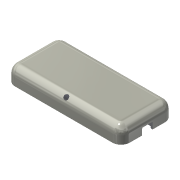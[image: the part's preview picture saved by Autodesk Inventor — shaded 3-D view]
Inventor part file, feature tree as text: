
AUTODESK INVENTOR PART (.ipt)
format: ipt  version: 2022.1 (Build 261234020, 234B)  size: 246,272 bytes
history: native  units: mm
features: extrude x6, fillet x5, sketch x4, plane x2, other x1, projected_geometry x1
ambient origin geometry x8: Origin, YZ Plane, XZ Plane, XY Plane, X Axis, Y Axis, Z Axis, Center Point
bodies: Solid1 (feature_tree)
feature tree (19):
  sketch  "Sketch1"  dims[d0=120.0mm d1=55.0mm]
  extrude  "Extrusion1"  Depth=55.0mm
  extrude  "Extrusion2"  Depth=10.0mm
  fillet  "Fillet3"  Radius=15.0mm
  fillet  "Fillet4"  Radius=10.0mm
  fillet  "Fillet5"  Radius=9.0mm
  other  "Lip3"
  fillet  "Fillet6"  Radius=9.0mm
  extrude  "Extrusion6"  Depth=10.0mm
  fillet  "Fillet7"  Radius=5.5mm
  extrude  "Extrusion7"  Depth=10.0mm
  plane  "Work Plane1"
  plane  "Work Plane2"
  sketch  "Sketch9"  dims[d32=2.0mm d33=2.0mm d34=0.0mm d35=0.0mm d36=0.872665mm d37=0.0mm d38=9.0mm d39=5.5mm d40=11.0mm d41=2.0mm d42=1.0mm d43=7.0mm d44=6.0mm d45=0.0mm d46=1.0mm d47=3.5mm d48=11.0mm d49=0.0mm d50=225.0deg d54=45.0deg d55=18.0mm d56=5.0mm d60=11.0mm d61=0.0mm d62=5.0mm d63=10.0mm d64=0.0mm d8=0.5mm d9=0.872665mm d16=0.5mm d17=0.872665mm d18=0.5mm d19=0.872665mm d22=0.0mm d23=0.0mm d24=0.0mm d25=0.0mm]
  extrude  "Extrusion10"  Depth=10.0mm
  extrude  "Extrusion11"  Depth=10.0mm
  sketch  "Sketch6"  dims[d2=5.0mm d3=5.0mm d4=15.0mm d5=0.0mm d6=10.0mm d7=0.0mm d29=9.0mm d30=9.0mm]
  sketch  "Sketch7"  dims[d31=9.0mm]
  projected_geometry  "Projected Loop1"
